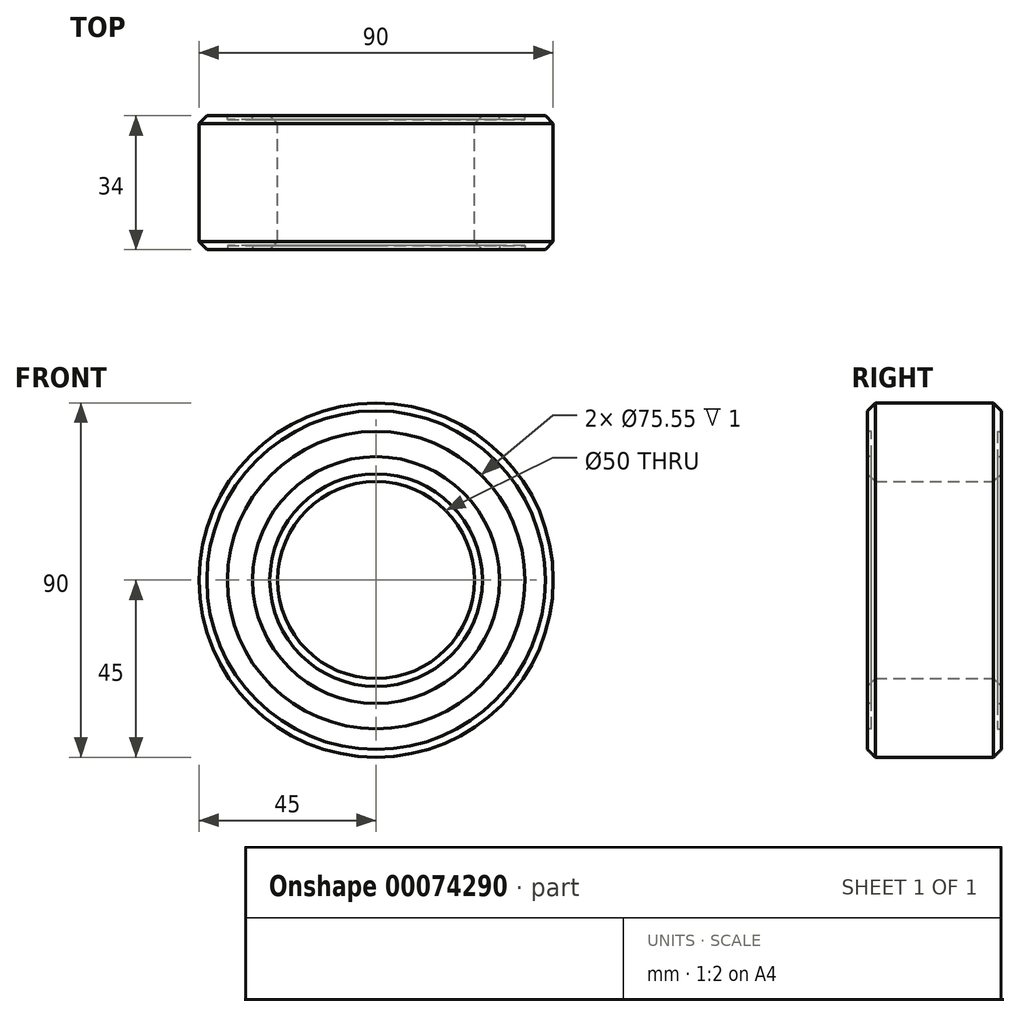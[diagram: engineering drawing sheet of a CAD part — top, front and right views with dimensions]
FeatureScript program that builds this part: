
annotation { "Feature Type Name" : "Feature", "Feature Type Description" : "" }
export const myFeature = defineFeature(function(context is Context, id is Id, definition is map)
    precondition{}
    {
        {
            var Q0;
            Q0=qCreatedBy(makeId("Front.planeOp"),FACE);
            var sketch = newSketch(context, id + "F0", { "sketchPlane" : qUnion([Q0])});
            skCircle(sketch, "E0", {"center": v(0, 0) * mm, "radius": 45 * mm});
            skCircle(sketch, "E1", {"center": v(0, 0) * mm, "radius": 25 * mm});
            skSolve(sketch);
        }
        {
            var Q0;
            Q0 = qSketchRegion(id + "F0", true);
            extrude(context, id + "F1", {"entities" : qUnion([Q0]), "depth" : 34 * mm});
        }
        {
            var Q0;
            Q0=makeQuery(id+"F1.opExtrude","CAP_EDGE",EDGE,{"disambiguationData":[OSD([sQuery(id+"F0.wireOp",EDGE,"E0")])],"isStart":false});
            var Q1;
            Q1=makeQuery(id+"F1.opExtrude","CAP_EDGE",EDGE,{"disambiguationData":[OSD([sQuery(id+"F0.wireOp",EDGE,"E0")])],"isStart":true});
            chamfer(context, id + "F2", {"entities" : qUnion([Q0, Q1]), "width" : 2 * mm, "tangentPropagation" : true});
        }
        {
            var Q0;
            Q0=makeQuery(id+"F1.opExtrude","CAP_EDGE",EDGE,{"disambiguationData":[OSD([sQuery(id+"F0.wireOp",EDGE,"E1")])],"isStart":false});
            chamfer(context, id + "F3", {"entities" : qUnion([Q0]), "width" : 2 * mm, "tangentPropagation" : true});
        }
        {
            var Q0;
            Q0=makeQuery(id+"F1.opExtrude","CAP_EDGE",EDGE,{"disambiguationData":[OSD([sQuery(id+"F0.wireOp",EDGE,"E1")])],"isStart":true});
            chamfer(context, id + "F4", {"entities" : qUnion([Q0]), "width" : 2 * mm, "tangentPropagation" : true});
        }
        {
            var Q0;
            Q0=makeQuery(id+"F1.opExtrude","CAP_FACE",FACE,{"disambiguationData":[OSD([sQuery(id+"F0.wireOp",EDGE,"E0"),sQuery(id+"F0.wireOp",EDGE,"E1")])],"isStart":true});
            var sketch = newSketch(context, id + "F5", { "sketchPlane" : qUnion([Q0])});
            skCircle(sketch, "E2", {"center": v(0, 0) * mm, "radius": 31.35 * mm});
            skCircle(sketch, "E3", {"center": v(0, 0) * mm, "radius": 37.78 * mm});
            skSolve(sketch);
        }
        {
            var Q0;
            Q0 = qSketchRegion(id + "F5", true);
            extrude(context, id + "F6", {"entities" : qUnion([Q0]), "operationType" : NewBodyOperationType.REMOVE, "oppositeDirection" : true, "depth" : 1 * mm});
        }
        {
            var Q0;
            Q0=makeQuery(id+"F1.opExtrude","CAP_FACE",FACE,{"disambiguationData":[OSD([sQuery(id+"F0.wireOp",EDGE,"E0"),sQuery(id+"F0.wireOp",EDGE,"E1")])],"isStart":false});
            var sketch = newSketch(context, id + "F7", { "sketchPlane" : qUnion([Q0])});
            skCircle(sketch, "E4.0", {"center": v(0, 0) * mm, "radius": 37.78 * mm});
            skCircle(sketch, "E4.1", {"center": v(0, 0) * mm, "radius": 31.35 * mm});
            skSolve(sketch);
        }
        {
            var Q0;
            Q0 = qSketchRegion(id + "F7", true);
            extrude(context, id + "F8", {"entities" : qUnion([Q0]), "operationType" : NewBodyOperationType.REMOVE, "oppositeDirection" : true, "depth" : 1 * mm});
        }
    });
